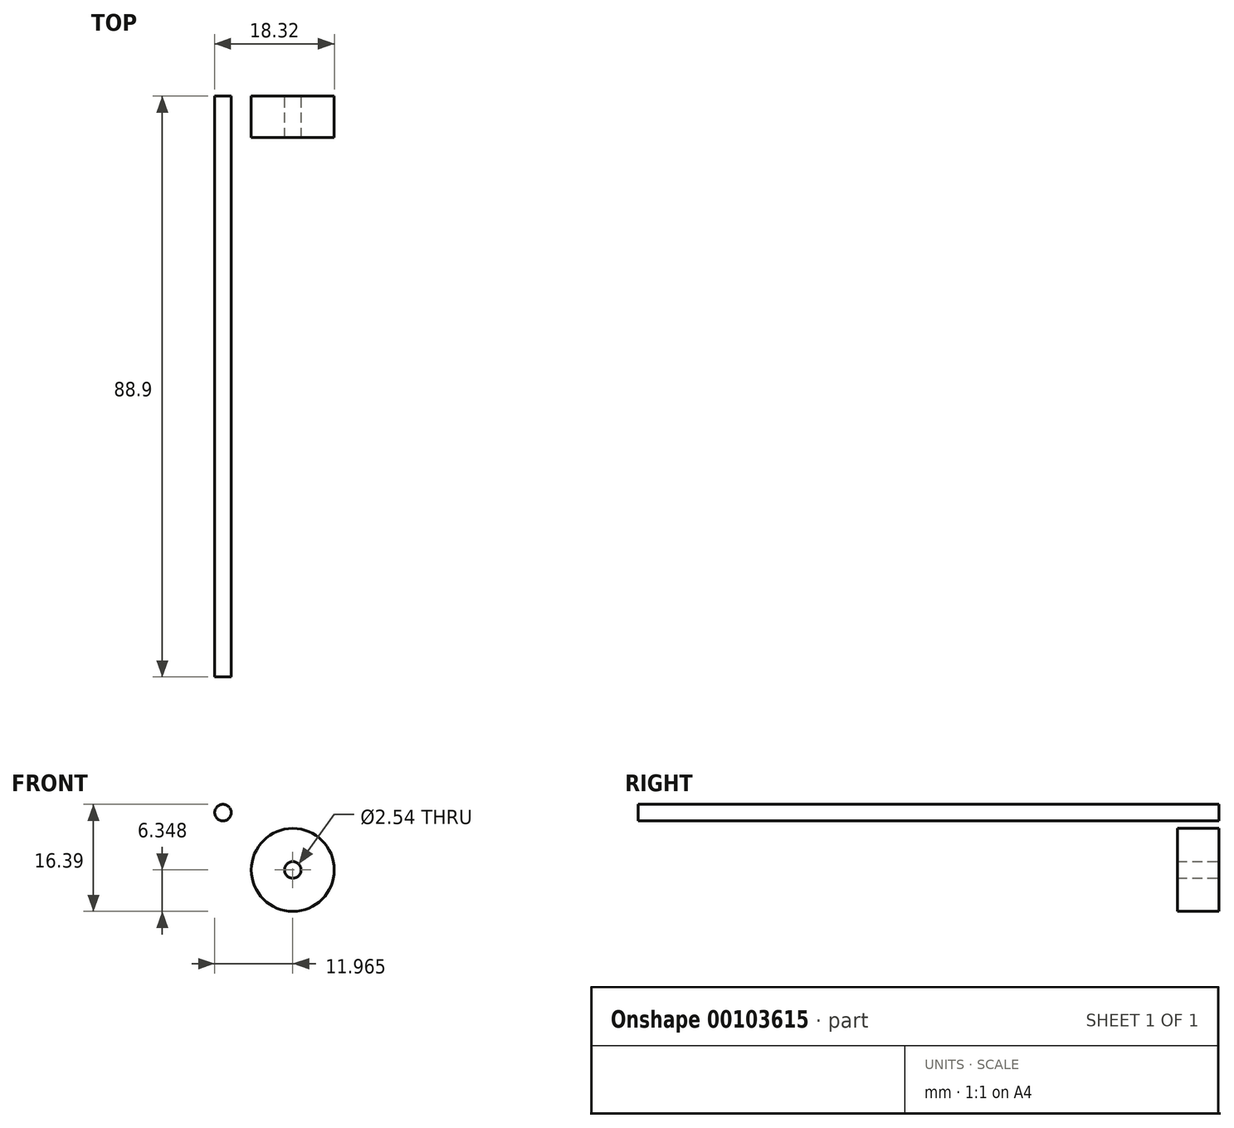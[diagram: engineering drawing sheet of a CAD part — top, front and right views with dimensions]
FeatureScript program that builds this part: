
annotation { "Feature Type Name" : "Feature", "Feature Type Description" : "" }
export const myFeature = defineFeature(function(context is Context, id is Id, definition is map)
    precondition{}
    {
        {
            var Q0;
            Q0=qCreatedBy(makeId("Front.planeOp"),FACE);
            var sketch = newSketch(context, id + "F0", { "sketchPlane" : qUnion([Q0])});
            skCircle(sketch, "E0", {"center": v(-54.47, 37.98) * mm, "radius": 1.27 * mm});
            skSolve(sketch);
        }
        {
            var Q0;
            Q0=makeQuery(id+"F0.imprint","IMPRINT",FACE,{"disambiguationData":[TD([[makeQuery(id+"F0.imprint","IMPRINT",EDGE,{"derivedFrom":sQuery(id+"F0.wireOp",EDGE,"E0")}),1.0]])]});
            extrude(context, id + "F1", {"entities" : qUnion([Q0]), "depth" : 88.9 * mm});
        }
        {
            var Q0;
            Q0=qCreatedBy(makeId("Front.planeOp"),FACE);
            var sketch = newSketch(context, id + "F2", { "sketchPlane" : qUnion([Q0])});
            skCircle(sketch, "E1", {"center": v(-43.77, 29.2) * mm, "radius": 6.35 * mm});
            skCircle(sketch, "E2", {"center": v(-43.77, 29.2) * mm, "radius": 1.27 * mm});
            skSolve(sketch);
        }
        {
            var Q0;
            Q0=makeQuery(id+"F2.imprint","IMPRINT",FACE,{"disambiguationData":[TD([[makeQuery(id+"F2.imprint","IMPRINT",EDGE,{"derivedFrom":sQuery(id+"F2.wireOp",EDGE,"E1")}),1.0]])]});
            extrude(context, id + "F3", {"entities" : qUnion([Q0]), "depth" : 6.35 * mm});
        }
    });
